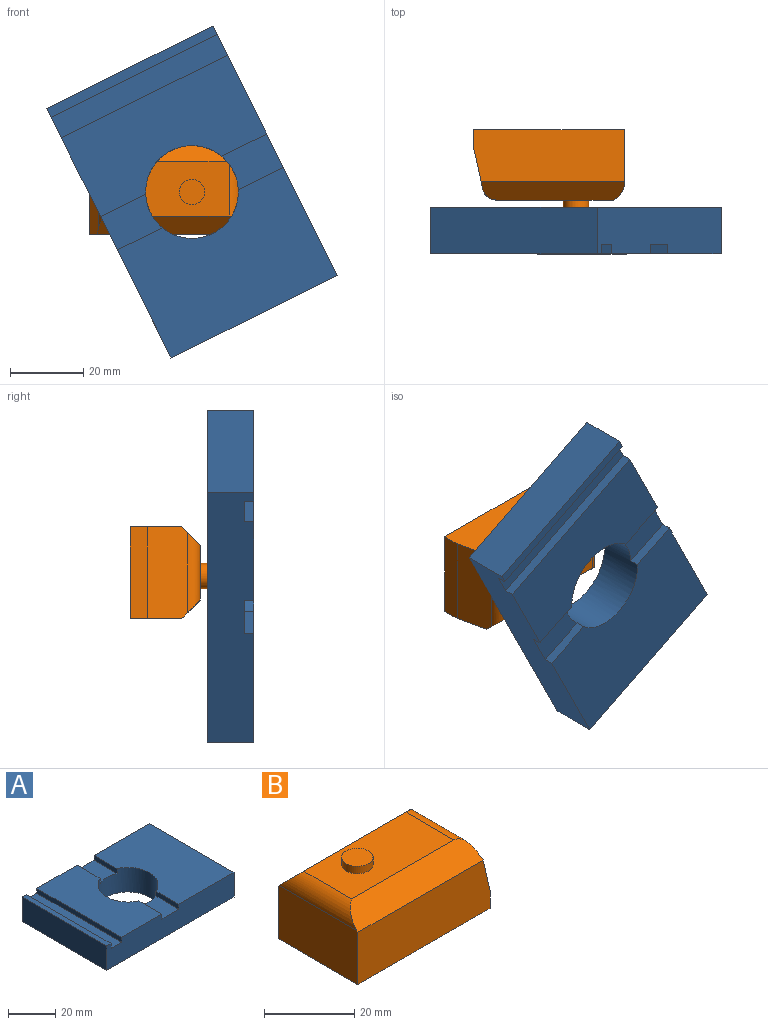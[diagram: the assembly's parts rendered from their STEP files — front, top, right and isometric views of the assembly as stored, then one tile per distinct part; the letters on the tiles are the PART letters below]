
ASSEMBLY  parts=2 mates=1
PART A: 18 faces, bbox 76.2x50.8x12.7 mm
  f0: plane 76.2x12.7mm, normal (0,-1,0), area 925.8mm2, adj f2,f3,f4,f6,f7,f8,f12,f13
  f1: cylinder r=12.7mm len=25.4mm, axis (0,0,-1), area 960.3mm2, adj f2,f7,f8,f9,f10,f11,f12,f13
  f2: plane 50.8x24.13mm, normal (0,0,1), area 1098mm2, adj f0,f1,f5,f9,f12,f16
  f3: plane 50.8x2.54mm, normal (0,0,1), area 129mm2, adj f0,f5,f6,f15
  f4: plane 50.8x12.7mm, normal (1,0,0), area 645.2mm2, adj f0,f5,f7,f8
  f5: plane 76.2x12.7mm, normal (0,1,0), area 925.8mm2, adj f2,f3,f4,f6,f7,f8,f9,f10
  f6: plane 50.8x12.7mm, normal (-1,0,0), area 645.2mm2, adj f0,f3,f5,f8
  f7: plane 50.8x33.02mm, normal (0,0,1), area 1549.6mm2, adj f0,f1,f4,f5,f10,f13
  f8: plane 76.2x50.8mm, normal (0,0,-1), area 3364.3mm2, adj f0,f1,f4,f5,f6
  f9: plane 13.76x2.54mm, normal (1,0,0), area 35mm2, adj f1,f2,f5,f11
  f10: plane 13.76x2.54mm, normal (-1,0,0), area 35mm2, adj f1,f5,f7,f11
  f11: plane 13.76x10.16mm, normal (0,0,1), area 132.6mm2, adj f1,f5,f9,f10
  f12: plane 13.76x2.54mm, normal (1,0,0), area 35mm2, adj f0,f1,f2,f14
  f13: plane 13.76x2.54mm, normal (-1,0,0), area 35mm2, adj f0,f1,f7,f14
  f14: plane 13.76x10.16mm, normal (0,0,1), area 132.6mm2, adj f0,f1,f12,f13
  f15: plane 50.8x2.54mm, normal (1,0,0), area 129mm2, adj f0,f3,f5,f17
  f16: plane 50.8x2.54mm, normal (-1,0,0), area 129mm2, adj f0,f2,f5,f17
  f17: plane 50.8x6.35mm, normal (0,0,1), area 322.6mm2, adj f0,f5,f15,f16
PART B: 13 faces, bbox 41.3x25x21.2 mm
  f0: plane 31.94x15mm, normal (0,0,1), area 441.3mm2, adj f1,f6,f9,f11,f12
  f1: cylinder r=5.08mm len=24.34mm, axis (0,1,0), area 112.8mm2, adj f0,f2,f11,f12
  f2: plane 25x14.5mm, normal (-1,0,0), area 362.3mm2, adj f1,f3,f7,f8,f11,f12
  f3: plane 41.28x25mm, normal (0,0,-1), area 1031.9mm2, adj f2,f4,f7,f8
  f4: plane 25x4.79mm, normal (1,0,0), area 119.8mm2, adj f3,f5,f7,f8
  f5: plane 25x10.93mm, normal (0.98,0,0.22), area 277.7mm2, adj f4,f6,f7,f8,f11,f12
  f6: cylinder r=3.83mm len=21.88mm, axis (0,1,0), area 98.3mm2, adj f0,f5,f11,f12
  f7: plane 41.28x14.16mm, normal (0,-1,0), area 574.8mm2, adj f2,f3,f4,f5,f12
  f8: plane 41.28x14.16mm, normal (0,1,0), area 574.8mm2, adj f2,f3,f4,f5,f11
  f9: cylinder r=3.47mm len=6.94mm, axis (0,0,-1), area 43.6mm2, adj f0,f10
  f10: plane 6.94x6.94mm, normal (0,0,1), area 37.8mm2, adj f9
  f11: plane 39.17x5mm, normal (0,0.71,0.71), area 264.9mm2, adj f0,f1,f2,f5,f6,f8
  f12: plane 39.17x5mm, normal (0,-0.71,0.71), area 264.9mm2, adj f0,f1,f2,f5,f6,f7
PLACE A rot(axis=(0.75,0.47,-0.47),106.1deg) t=(7.41,-21.16,-0.93)mm
PLACE B rot(axis=(0,-0.71,0.71),180deg) t=(-6.1,18.16,-12.5)mm
MATE revolute A.f1 <-> B.f9  axis (0,1,0) through (7.41,-21.16,-0.93)mm
